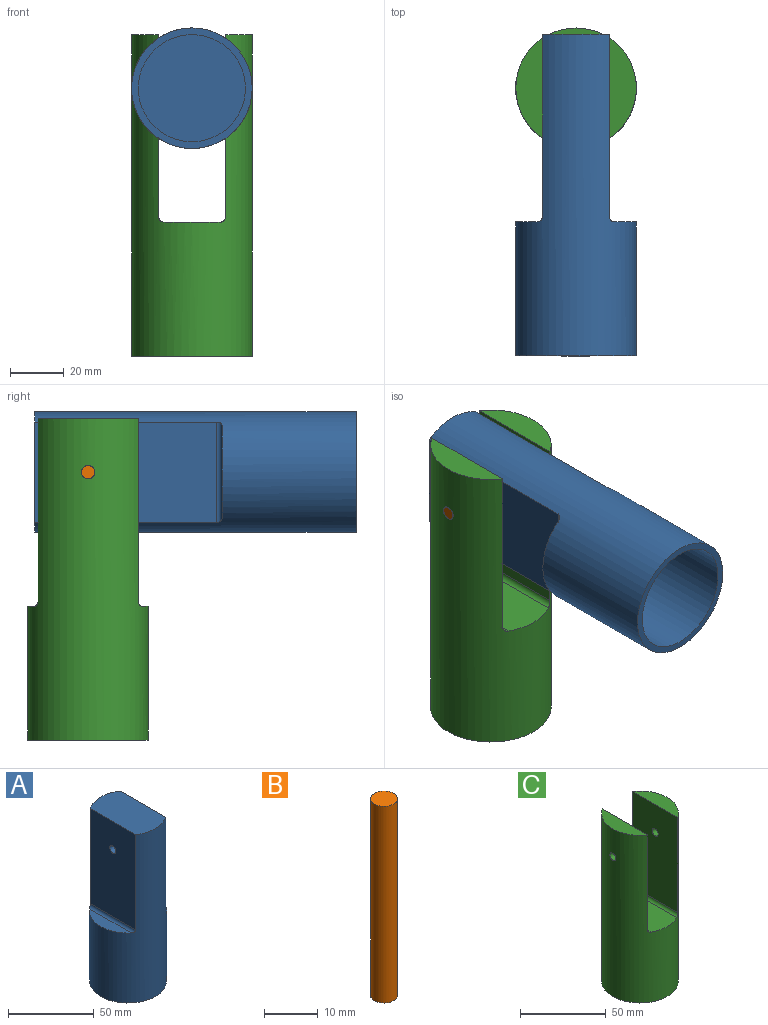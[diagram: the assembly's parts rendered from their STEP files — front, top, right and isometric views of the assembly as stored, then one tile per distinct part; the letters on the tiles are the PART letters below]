
ASSEMBLY  parts=3 mates=2
PART A: 12 faces, bbox 45x45x120 mm
  f0: plane 45x25mm, normal (0,0,1), area 1064.1mm2, adj f1,f3,f5
  f1: cylinder r=22.5mm len=120mm, axis (0,0,-1), area 10783.7mm2, adj f0,f2,f3,f4,f5,f6,f10,f11
  f2: plane 45x45mm, normal (0,0,-1), area 333.8mm2, adj f1,f7
  f3: plane 68x37.42mm, normal (-1,0,0), area 2524.7mm2, adj f0,f1,f9,f10
  f4: plane 34.41x8mm, normal (0,0,1), area 191.2mm2, adj f1,f10
  f5: plane 68x37.42mm, normal (1,0,0), area 2524.7mm2, adj f0,f1,f9,f11
  f6: plane 34.41x8mm, normal (0,0,1), area 191.2mm2, adj f1,f11
  f7: cylinder r=20mm len=40mm, axis (0,0,-1), area 4398.2mm2, adj f2,f8
  f8: plane 40x40mm, normal (0,0,-1), area 1256.6mm2, adj f7
  f9: cylinder r=2.5mm len=25mm, axis (1,0,0), area 392.7mm2, adj f3,f5
  f10: cylinder r=2mm len=37.42mm, axis (0,1,0), area 114.3mm2, adj f1,f3,f4
  f11: cylinder r=2mm len=37.42mm, axis (0,-1,0), area 114.3mm2, adj f1,f5,f6
PART B: 3 faces, bbox 5x5x45 mm
  f0: cylinder r=2.5mm len=45mm, axis (0,0,-1), area 706.9mm2, adj f1,f2
  f1: plane 5x5mm, normal (0,0,1), area 19.6mm2, adj f0
  f2: plane 5x5mm, normal (0,0,-1), area 19.6mm2, adj f0
PART C: 13 faces, bbox 45x45x120 mm
  f0: cylinder r=22.5mm len=120mm, axis (0,0,-1), area 13218.5mm2, adj f1,f2,f3,f4,f5,f6,f9,f10
  f1: plane 37.42x10mm, normal (0,0,1), area 263.2mm2, adj f0,f5
  f2: plane 37.42x10mm, normal (0,0,1), area 263.2mm2, adj f0,f4
  f3: plane 45x45mm, normal (0,0,-1), area 333.8mm2, adj f0,f7
  f4: plane 68x37.42mm, normal (1,0,0), area 2524.7mm2, adj f0,f2,f10,f11
  f5: plane 68x37.42mm, normal (-1,0,0), area 2524.7mm2, adj f0,f1,f9,f12
  f6: plane 45x21mm, normal (0,0,1), area 909.5mm2, adj f0,f11,f12
  f7: cylinder r=20mm len=40mm, axis (0,0,-1), area 4398.2mm2, adj f3,f8
  f8: plane 40x40mm, normal (0,0,-1), area 1256.6mm2, adj f7
  f9: cylinder r=2.5mm len=10mm, axis (1,0,0), area 156mm2, adj f0,f5
  f10: cylinder r=2.5mm len=10mm, axis (1,0,0), area 156mm2, adj f0,f4
  f11: cylinder r=2mm len=39.8mm, axis (0,-1,0), area 120.4mm2, adj f0,f4,f6
  f12: cylinder r=2mm len=39.8mm, axis (0,1,0), area 120.4mm2, adj f0,f5,f6
PLACE A rot(axis=(-1,0,0),90deg) t=(31.33,-41.17,111.32)mm
PLACE B rot(axis=(-0.58,-0.58,0.58),120deg) t=(53.83,58.83,111.32)mm
PLACE C t=(31.39,58.83,11.32)mm fixed
MATE fastened B.f0 <-> C.f9  axis (1,0,0) through (8.83,58.83,111.32)mm
MATE fastened B.f0 <-> A.f9  axis (1,0,0) through (31.33,58.83,111.32)mm
